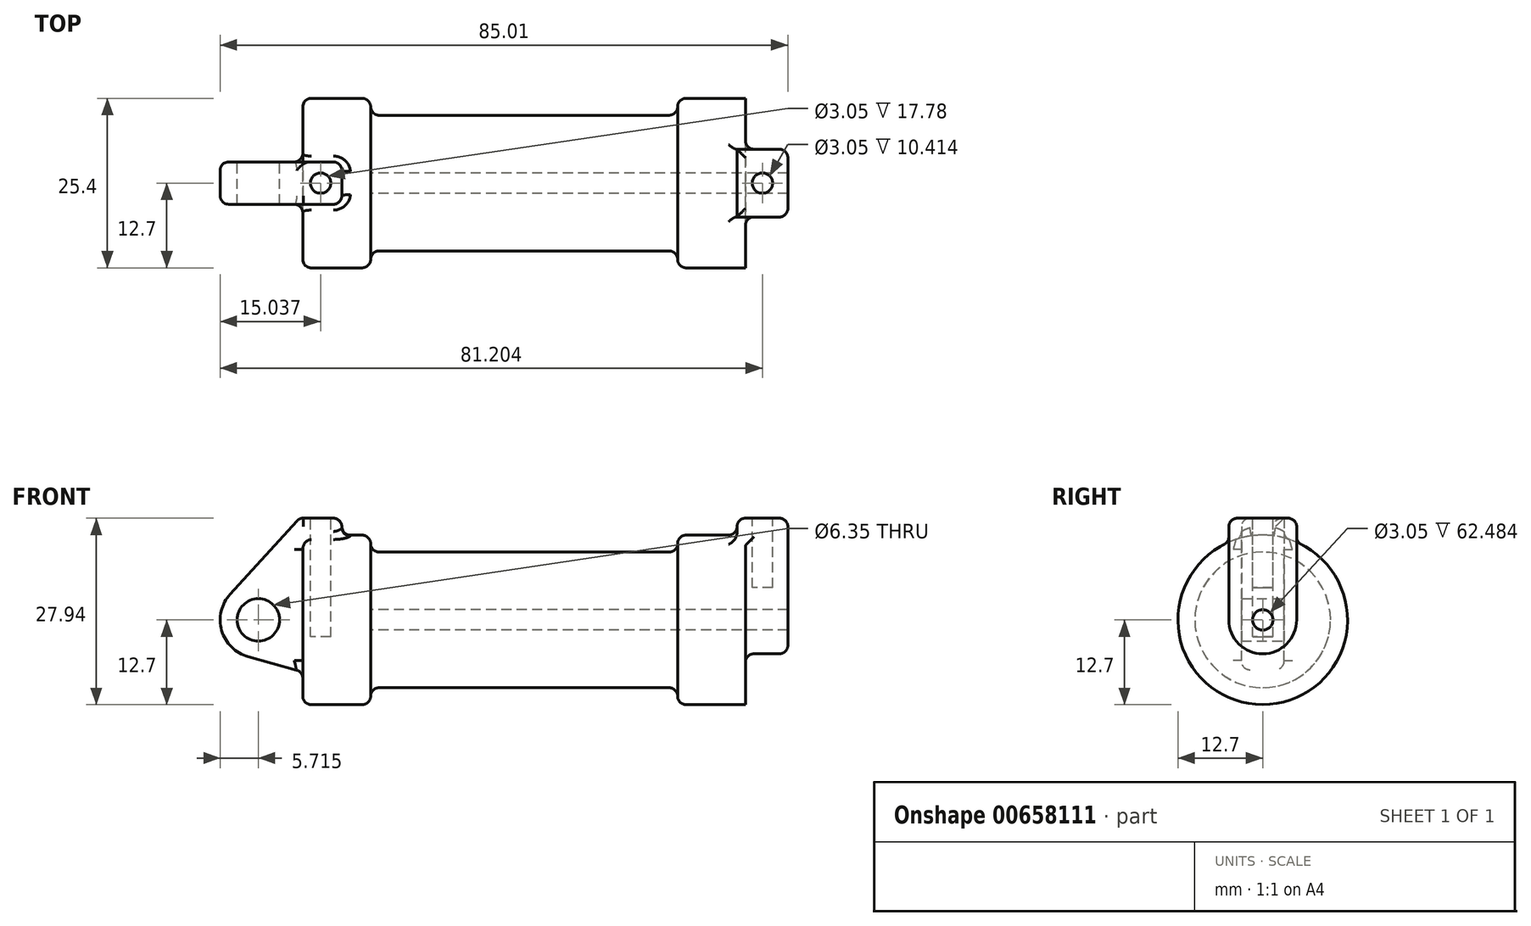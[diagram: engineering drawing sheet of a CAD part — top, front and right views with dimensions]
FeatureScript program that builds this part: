
annotation { "Feature Type Name" : "Feature", "Feature Type Description" : "" }
export const myFeature = defineFeature(function(context is Context, id is Id, definition is map)
    precondition{}
    {
        {
            var Q0;
            Q0=qCreatedBy(makeId("Front.planeOp"),FACE);
            var sketch = newSketch(context, id + "F0", { "sketchPlane" : qUnion([Q0])});
            skLineSegment(sketch, "E0", {"start": v(0, 0) * mm, "end": v(0, 12.7) * mm});
            skLineSegment(sketch, "E1", {"start": v(0, 12.7) * mm, "end": v(10.16, 12.7) * mm});
            skLineSegment(sketch, "E2", {"start": v(10.16, 12.7) * mm, "end": v(10.16, 10.16) * mm});
            skLineSegment(sketch, "E3", {"start": v(10.16, 10.16) * mm, "end": v(56.13, 10.16) * mm});
            skLineSegment(sketch, "E4", {"start": v(56.13, 10.16) * mm, "end": v(56.13, 12.7) * mm});
            skLineSegment(sketch, "E5", {"start": v(56.13, 12.7) * mm, "end": v(66.3, 12.7) * mm});
            skLineSegment(sketch, "E6", {"start": v(66.3, 12.7) * mm, "end": v(66.3, 0) * mm});
            skLineSegment(sketch, "E7", {"start": v(66.3, 0) * mm, "end": v(0, 0) * mm});
            skLineSegment(sketch, "E8", {"start": v(5.84, 15.24) * mm, "end": v(-0.5, 15.24) * mm});
            skLineSegment(sketch, "E9", {"start": v(-0.5, 15.24) * mm, "end": v(-10.88, 3.85) * mm});
            skLineSegment(sketch, "E10", {"start": v(0, 0) * mm, "end": v(-6.65, 0) * mm});
            skCircle(sketch, "E11", {"center": v(-6.65, 0) * mm, "radius": 5.72 * mm});
            skCircle(sketch, "E12", {"center": v(-6.65, 0) * mm, "radius": 3.18 * mm});
            skLineSegment(sketch, "E13", {"start": v(5.84, 15.24) * mm, "end": v(5.84, -9.4) * mm});
            skLineSegment(sketch, "E14", {"start": v(5.84, -9.4) * mm, "end": v(-8.18, -5.5) * mm});
            skSolve(sketch);
        }
        {
            var Q0;
            {var subQ1=sQuery(id+"F0.wireOp",EDGE,"E0");Q0=makeQuery(id+"F0.imprint","IMPRINT",FACE,{"disambiguationData":[TD([[makeQuery(id+"F0.imprint","IMPRINT",EDGE,{"derivedFrom":subQ1}),1.0]])]});}
            var Q1;
            {var subQ5=sQuery(id+"F0.wireOp",EDGE,"E12");Q1=makeQuery(id+"F0.imprint","IMPRINT",FACE,{"disambiguationData":[TD([[makeQuery(id+"F0.imprint","IMPRINT",EDGE,{"derivedFrom":subQ5}),-1.0]])]});}
            var Q2;
            {var subQ0=sQuery(id+"F0.wireOp",EDGE,"E0");Q2=makeQuery(id+"F0.imprint","IMPRINT",FACE,{"disambiguationData":[TD([[makeQuery(id+"F0.imprint","IMPRINT",EDGE,{"derivedFrom":subQ0}),-1.0]])]});}
            var Q3;
            {var subQ0=sQuery(id+"F0.wireOp",EDGE,"E14");Q3=makeQuery(id+"F0.imprint","IMPRINT",FACE,{"disambiguationData":[TD([[makeQuery(id+"F0.imprint","IMPRINT",EDGE,{"derivedFrom":subQ0}),-1.0]])]});}
            extrude(context, id + "F1", {"entities" : qUnion([Q0, Q1, Q2, Q3]), "endBound" : BoundingType.SYMMETRIC, "depth" : 6.35 * mm, "offsetDistance" : 25.4 * mm});
        }
        {
            var Q0;
            {var subQ0=sQuery(id+"F0.wireOp",EDGE,"E2");Q0=makeQuery(id+"F0.imprint","IMPRINT",FACE,{"disambiguationData":[TD([[makeQuery(id+"F0.imprint","IMPRINT",EDGE,{"derivedFrom":subQ0}),-1.0]])]});}
            var Q1;
            {var subQ0=sQuery(id+"F0.wireOp",EDGE,"E0");Q1=makeQuery(id+"F0.imprint","IMPRINT",FACE,{"disambiguationData":[TD([[makeQuery(id+"F0.imprint","IMPRINT",EDGE,{"derivedFrom":subQ0}),-1.0]])]});}
            var Q2;
            Q2=sQuery(id+"F0.wireOp",EDGE,"E7");
            revolve(context, id + "F2", {"entities" : qUnion([Q0, Q1]), "axis" : qUnion([Q2]), "revolveType" : RevolveType.FULL});
        }
        {
            var Q0;
            Q0=makeQuery(id+"F2.opRevolve","SWEPT_FACE",FACE,{"disambiguationData":[OSD([sQuery(id+"F0.wireOp",EDGE,"E6")])]});
            var sketch = newSketch(context, id + "F3", { "sketchPlane" : qUnion([Q0])});
            skCircle(sketch, "E15", {"center": v(0, 0) * mm, "radius": 1.52 * mm});
            skCircle(sketch, "E16", {"center": v(0, 0) * mm, "radius": 5.08 * mm});
            skLineSegment(sketch, "E17", {"start": v(5.08, 0) * mm, "end": v(5.08, 15.24) * mm});
            skLineSegment(sketch, "E18", {"start": v(-5.08, 0) * mm, "end": v(-5.08, 15.24) * mm});
            skLineSegment(sketch, "E19", {"start": v(5.08, 15.24) * mm, "end": v(-5.08, 15.24) * mm});
            skSolve(sketch);
        }
        {
            var Q0;
            Q0=makeQuery(id+"F3.imprint","IMPRINT",FACE,{"disambiguationData":[TD([[makeQuery(id+"F3.imprint","IMPRINT",EDGE,{"derivedFrom":sQuery(id+"F3.wireOp",EDGE,"E15")}),-1.0]])]});
            var Q1;
            {var subQ0=sQuery(id+"F3.wireOp",EDGE,"kBfzXfzW-diKN-qLCQ-soDv-WeQLsgFTbgrA");Q1=makeQuery(id+"F3.imprint","IMPRINT",FACE,{"disambiguationData":[TD([[makeQuery(id+"F3.imprint","IMPRINT",EDGE,{"derivedFrom":subQ0}),-1.0]])]});}
            extrude(context, id + "F4", {"entities" : qUnion([Q0, Q1]), "operationType" : NewBodyOperationType.ADD, "depth" : 6.35 * mm, "offsetDistance" : 25.4 * mm, "hasSecondDirection" : true, "secondDirectionOppositeDirection" : true, "secondDirectionDepth" : 1.27 * mm});
        }
        {
            var Q0;
            Q0=makeQuery(id+"F4.boolean.opBoolean","SPLIT",FACE,{"disambiguationData":[TD([makeQuery(id+"F4.opExtrude","SWEPT_FACE",FACE,{"disambiguationData":[OSD([sQuery(id+"F3.wireOp",EDGE,"E15")])]})])],"derivedFrom":makeQuery(id+"F2.opRevolve","SWEPT_FACE",FACE,{"disambiguationData":[OSD([sQuery(id+"F0.wireOp",EDGE,"E6")])]})});
            var Q1;
            Q1=makeQuery(id+"F2.opRevolve","SWEPT_FACE",FACE,{"disambiguationData":[OSD([sQuery(id+"F0.wireOp",EDGE,"E2")])]});
            extrude(context, id + "F5", {"entities" : qUnion([Q0]), "operationType" : NewBodyOperationType.REMOVE, "endBound" : BoundingType.UP_TO_SURFACE, "oppositeDirection" : true, "depth" : 25.4 * mm, "endBoundEntityFace" : qUnion([Q1]), "offsetDistance" : 25.4 * mm});
        }
        {
            var Q0;
            Q0 = qSketchRegion(id + "F3", true);
            extrude(context, id + "F6", {"entities" : qUnion([Q0]), "operationType" : NewBodyOperationType.ADD, "depth" : 6.35 * mm, "offsetDistance" : 25.4 * mm, "hasSecondDirection" : true, "secondDirectionOppositeDirection" : true, "secondDirectionDepth" : 1.27 * mm});
        }
        {
            var Q0;
            Q0=makeQuery(id+"F6.opExtrude","SWEPT_FACE",FACE,{"disambiguationData":[OSD([sQuery(id+"F3.wireOp",EDGE,"E19")])]});
            var sketch = newSketch(context, id + "F7", { "sketchPlane" : qUnion([Q0])});
            skCircle(sketch, "E20", {"center": v(68.83, 0) * mm, "radius": 1.52 * mm});
            skSolve(sketch);
        }
        {
            var Q0;
            Q0=makeQuery(id+"F7.imprint","IMPRINT",FACE,{"disambiguationData":[TD([[makeQuery(id+"F7.imprint","IMPRINT",EDGE,{"derivedFrom":sQuery(id+"F7.wireOp",EDGE,"E20")}),1.0]])]});
            var Q1;
            Q1=sQuery(id+"F7.wireOp",EDGE,"E20");
            extrude(context, id + "F8", {"entities" : qUnion([Q0]), "operationType" : NewBodyOperationType.REMOVE, "surfaceEntities" : qUnion([Q1]), "oppositeDirection" : true, "depth" : 10.4 * mm, "offsetDistance" : 25.4 * mm});
        }
        {
            var Q0;
            Q0=makeQuery(id+"F1.opExtrude","SWEPT_FACE",FACE,{"disambiguationData":[OSD([sQuery(id+"F0.wireOp",EDGE,"E8")])]});
            var sketch = newSketch(context, id + "F9", { "sketchPlane" : qUnion([Q0])});
            skCircle(sketch, "E21", {"center": v(2.67, 0) * mm, "radius": 1.52 * mm});
            skPoint(sketch, "E21.centerSnap0", {"position": v(5.84, 0) * mm});
            skPoint(sketch, "E21.centerSnap1", {"position": v(2.67, -3.18) * mm});
            skSolve(sketch);
        }
        {
            var Q0;
            Q0=makeQuery(id+"F9.imprint","IMPRINT",FACE,{"disambiguationData":[TD([[makeQuery(id+"F9.imprint","IMPRINT",EDGE,{"derivedFrom":sQuery(id+"F9.wireOp",EDGE,"E21")}),1.0]])]});
            extrude(context, id + "F10", {"entities" : qUnion([Q0]), "operationType" : NewBodyOperationType.REMOVE, "oppositeDirection" : true, "depth" : 17.78 * mm, "offsetDistance" : 25.4 * mm});
        }
        {
            var Q0;
            Q0=makeQuery(id+"F2.opRevolve","SWEPT_EDGE",EDGE,{"disambiguationData":[OSD([sQuery(id+"F0.wireOp",EDGE,"E2"),sQuery(id+"F0.wireOp",EDGE,"E3")])]});
            var Q1;
            Q1=makeQuery(id+"F2.opRevolve","SWEPT_EDGE",EDGE,{"disambiguationData":[OSD([sQuery(id+"F0.wireOp",EDGE,"E1"),sQuery(id+"F0.wireOp",EDGE,"E2")])]});
            var Q2;
            Q2=makeQuery(id+"F1.opExtrude","SWEPT_EDGE",EDGE,{"disambiguationData":[OSD([sQuery(id+"F0.wireOp",EDGE,"E8"),sQuery(id+"F0.wireOp",EDGE,"E13")])]});
            var Q3;
            Q3=makeQuery(id+"F1.opExtrude","CAP_EDGE",EDGE,{"disambiguationData":[OSD([sQuery(id+"F0.wireOp",EDGE,"E13")])],"isStart":true});
            var Q4;
            Q4=makeQuery(id+"F1.opExtrude","CAP_EDGE",EDGE,{"disambiguationData":[OSD([sQuery(id+"F0.wireOp",EDGE,"E13")])],"isStart":false});
            var Q5;
            Q5=makeQuery(id+"F1.opExtrude","CAP_EDGE",EDGE,{"disambiguationData":[OSD([sQuery(id+"F0.wireOp",EDGE,"E8")])],"isStart":false});
            var Q6;
            Q6=makeQuery(id+"F2.opRevolve","SWEPT_FACE",FACE,{"disambiguationData":[OSD([sQuery(id+"F0.wireOp",EDGE,"E1")])]});
            fillet(context, id + "F11", {"entities" : qUnion([Q0, Q1, Q2, Q3, Q4, Q5, Q6]), "radius" : 1.27 * mm, "tangentPropagation" : true, "allowEdgeOverflow" : false});
        }
        {
            var Q0;
            Q0=makeQuery(id+"F1.opExtrude","SWEPT_FACE",FACE,{"disambiguationData":[OSD([sQuery(id+"F0.wireOp",EDGE,"E13")])]});
            fillet(context, id + "F12", {"entities" : qUnion([Q0]), "radius" : 1.27 * mm, "tangentPropagation" : true, "allowEdgeOverflow" : false});
        }
        {
            var Q0;
            Q0=makeQuery(id+"F2.opRevolve","SWEPT_FACE",FACE,{"disambiguationData":[OSD([sQuery(id+"F0.wireOp",EDGE,"E4")])]});
            fillet(context, id + "F13", {"entities" : qUnion([Q0]), "radius" : 1.27 * mm, "tangentPropagation" : true, "allowEdgeOverflow" : false});
        }
        {
            var Q0;
            Q0=makeQuery(id+"F6.opExtrude","CAP_EDGE",EDGE,{"disambiguationData":[OSD([sQuery(id+"F3.wireOp",EDGE,"E19")])],"isStart":false});
            var Q1;
            Q1=makeQuery(id+"F6.opExtrude","SWEPT_EDGE",EDGE,{"disambiguationData":[OSD([sQuery(id+"F3.wireOp",EDGE,"E18"),sQuery(id+"F3.wireOp",EDGE,"E19")])]});
            var Q2;
            Q2=makeQuery(id+"F6.opExtrude","CAP_EDGE",EDGE,{"disambiguationData":[OSD([sQuery(id+"F3.wireOp",EDGE,"E19")])],"isStart":true});
            var Q3;
            Q3=makeQuery(id+"F6.opExtrude","SWEPT_EDGE",EDGE,{"disambiguationData":[OSD([sQuery(id+"F3.wireOp",EDGE,"E17"),sQuery(id+"F3.wireOp",EDGE,"E19")])]});
            var Q4;
            Q4=makeQuery(id+"F6.opExtrude","CAP_EDGE",EDGE,{"disambiguationData":[OSD([sQuery(id+"F3.wireOp",EDGE,"E17")])],"isStart":false});
            var Q5;
            Q5=makeQuery(id+"F4.opExtrude","CAP_EDGE",EDGE,{"disambiguationData":[OSD([sQuery(id+"F3.wireOp",EDGE,"E16")])],"isStart":false});
            var Q6;
            Q6=makeQuery(id+"F6.boolean.opBoolean","INTERSECT",EDGE,{"derivedFrom":[makeQuery(id+"F4.boolean.opBoolean","SPLIT",FACE,{"disambiguationData":[TD([makeQuery(id+"F2.opRevolve","SWEPT_FACE",FACE,{"disambiguationData":[OSD([sQuery(id+"F0.wireOp",EDGE,"E5")])]})])],"derivedFrom":makeQuery(id+"F2.opRevolve","SWEPT_FACE",FACE,{"disambiguationData":[OSD([sQuery(id+"F0.wireOp",EDGE,"E6")])]})}),makeQuery(id+"F6.opExtrude","SWEPT_FACE",FACE,{"disambiguationData":[OSD([sQuery(id+"F3.wireOp",EDGE,"E18")])]})]});
            var Q7;
            Q7=makeQuery(id+"F6.boolean.opBoolean","INTERSECT",EDGE,{"derivedFrom":[makeQuery(id+"F2.opRevolve","SWEPT_FACE",FACE,{"disambiguationData":[OSD([sQuery(id+"F0.wireOp",EDGE,"E5")])]}),makeQuery(id+"F6.opExtrude","SWEPT_FACE",FACE,{"disambiguationData":[OSD([sQuery(id+"F3.wireOp",EDGE,"E18")])]})]});
            var Q8;
            Q8=makeQuery(id+"F6.boolean.opBoolean","INTERSECT",EDGE,{"derivedFrom":[makeQuery(id+"F2.opRevolve","SWEPT_FACE",FACE,{"disambiguationData":[OSD([sQuery(id+"F0.wireOp",EDGE,"E5")])]}),makeQuery(id+"F6.opExtrude","CAP_FACE",FACE,{"disambiguationData":[OSD([sQuery(id+"F3.wireOp",EDGE,"E15"),sQuery(id+"F3.wireOp",EDGE,"E16"),sQuery(id+"F3.wireOp",EDGE,"E17"),sQuery(id+"F3.wireOp",EDGE,"E18"),sQuery(id+"F3.wireOp",EDGE,"E19")])],"isStart":true})]});
            var Q9;
            Q9=makeQuery(id+"F2.opRevolve","SWEPT_FACE",FACE,{"disambiguationData":[OSD([sQuery(id+"F0.wireOp",EDGE,"E1")])]});
            var Q10;
            {var subQ0=sQuery(id+"F0.wireOp",EDGE,"E0");Q10=makeQuery(id+"F11.opFillet","BLEND_EDGE",EDGE,{"blendedFrom":[makeQuery(id+"F2.opRevolve","SWEPT_EDGE",EDGE,{"disambiguationData":[OSD([subQ0,sQuery(id+"F0.wireOp",EDGE,"E1")])]}),makeQuery(id+"F2.opRevolve","SWEPT_FACE",FACE,{"disambiguationData":[OSD([subQ0])]})],"blendedInto":[makeQuery(id+"F2.opRevolve","SWEPT_FACE",FACE,{"disambiguationData":[OSD([subQ0])]})]});}
            var Q11;
            Q11=makeQuery(id+"F6.boolean.opBoolean","INTERSECT",EDGE,{"derivedFrom":[makeQuery(id+"F2.opRevolve","SWEPT_FACE",FACE,{"disambiguationData":[OSD([sQuery(id+"F0.wireOp",EDGE,"E5")])]}),makeQuery(id+"F6.opExtrude","SWEPT_FACE",FACE,{"disambiguationData":[OSD([sQuery(id+"F3.wireOp",EDGE,"E17")])]})]});
            fillet(context, id + "F14", {"entities" : qUnion([Q0, Q1, Q2, Q3, Q4, Q5, Q6, Q7, Q8, Q9, Q10, Q11]), "radius" : 1.27 * mm, "tangentPropagation" : true, "allowEdgeOverflow" : false});
        }
        {
            var Q0;
            Q0=makeQuery(id+"F1.opExtrude","SWEPT_BODY",BODY,{"disambiguationData":[OSD([sQuery(id+"F0.wireOp",EDGE,"E8"),sQuery(id+"F0.wireOp",EDGE,"E9"),sQuery(id+"F0.wireOp",EDGE,"E11"),sQuery(id+"F0.wireOp",EDGE,"E12"),sQuery(id+"F0.wireOp",EDGE,"E13"),sQuery(id+"F0.wireOp",EDGE,"E14")])]});
            var Q1;
            Q1=makeQuery(id+"F2.opRevolve","SWEPT_BODY",BODY,{"disambiguationData":[OSD([sQuery(id+"F0.wireOp",EDGE,"E0"),sQuery(id+"F0.wireOp",EDGE,"E1"),sQuery(id+"F0.wireOp",EDGE,"E2"),sQuery(id+"F0.wireOp",EDGE,"E3"),sQuery(id+"F0.wireOp",EDGE,"E4"),sQuery(id+"F0.wireOp",EDGE,"E5"),sQuery(id+"F0.wireOp",EDGE,"E6"),sQuery(id+"F0.wireOp",EDGE,"E7")])]});
            booleanBodies(context, id + "F15", {"operationType" : BooleanOperationType.UNION, "tools" : qUnion([Q0, Q1])});
        }
        {
            var Q0;
            Q0=makeQuery(id+"F15.opBoolean","INTERSECT",EDGE,{"derivedFrom":[makeQuery(id+"F2.opRevolve","SWEPT_FACE",FACE,{"disambiguationData":[OSD([sQuery(id+"F0.wireOp",EDGE,"E1")])]}),makeQuery(id+"F1.opExtrude","CAP_FACE",FACE,{"disambiguationData":[OSD([sQuery(id+"F0.wireOp",EDGE,"E8"),sQuery(id+"F0.wireOp",EDGE,"E9"),sQuery(id+"F0.wireOp",EDGE,"E11"),sQuery(id+"F0.wireOp",EDGE,"E12"),sQuery(id+"F0.wireOp",EDGE,"E13"),sQuery(id+"F0.wireOp",EDGE,"E14")])],"isStart":false})]});
            fillet(context, id + "F16", {"entities" : qUnion([Q0]), "radius" : 1.27 * mm, "tangentPropagation" : true, "allowEdgeOverflow" : false});
        }
    });
